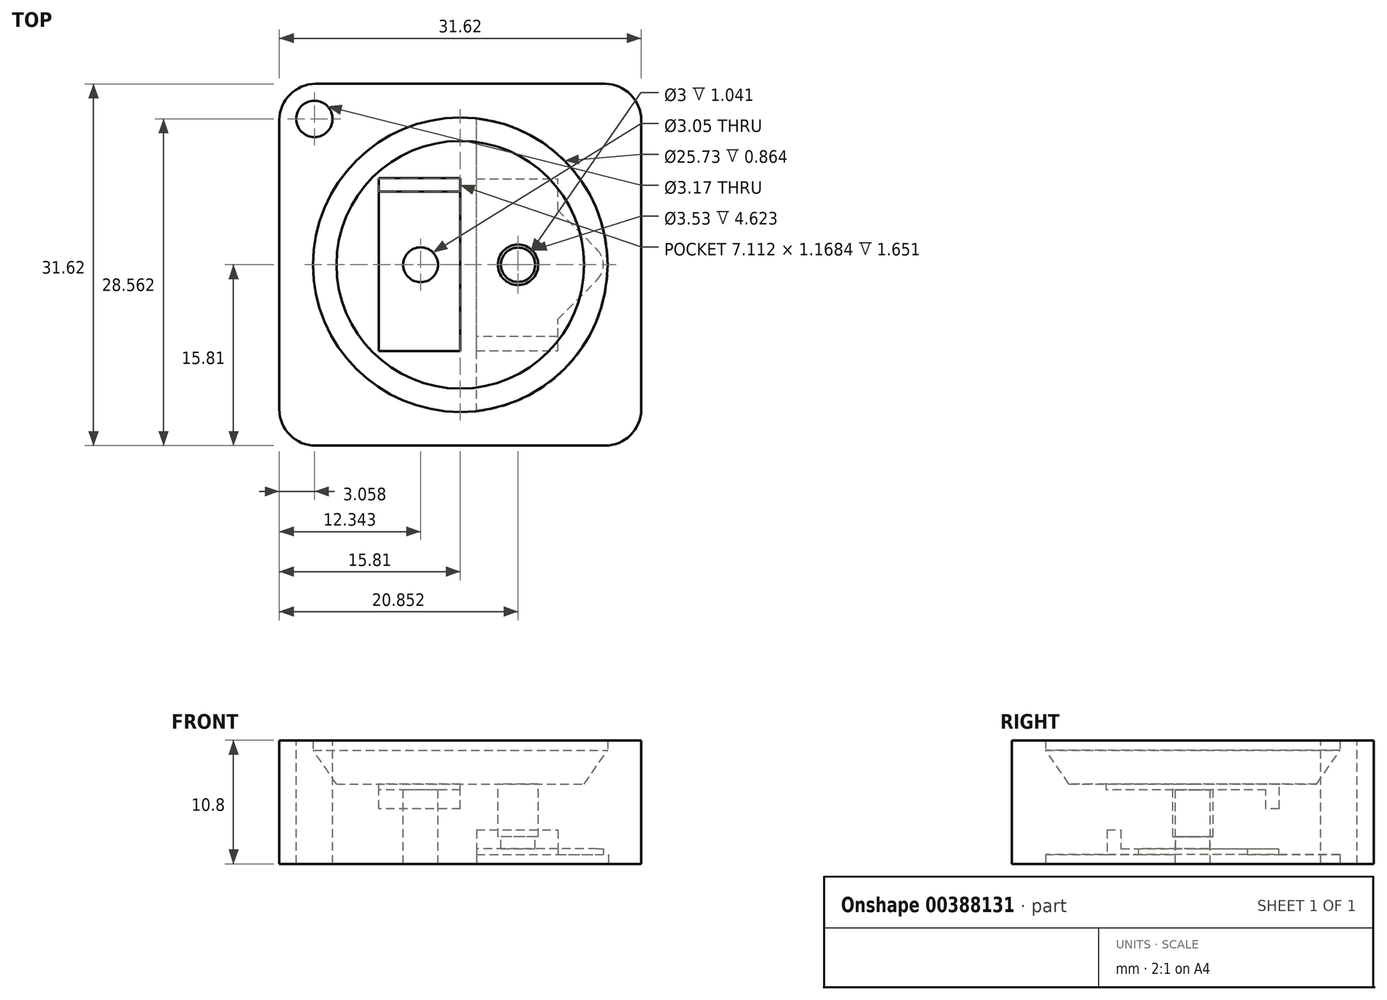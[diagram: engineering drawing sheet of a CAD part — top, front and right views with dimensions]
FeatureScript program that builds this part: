
annotation { "Feature Type Name" : "Feature", "Feature Type Description" : "" }
export const myFeature = defineFeature(function(context is Context, id is Id, definition is map)
    precondition{}
    {
        {
            var Q0;
            Q0=qCreatedBy(makeId("Top.planeOp"),FACE);
            var sketch = newSketch(context, id + "F0", { "sketchPlane" : qUnion([Q0])});
            skLineSegment(sketch, "E0.bottom", {"start": v(-12.64, 15.81) * mm, "end": v(12.64, 15.81) * mm});
            skLineSegment(sketch, "E0.top", {"start": v(-12.64, -15.81) * mm, "end": v(12.64, -15.81) * mm});
            skLineSegment(sketch, "E0.left", {"start": v(-15.81, 12.64) * mm, "end": v(-15.81, -12.64) * mm});
            skLineSegment(sketch, "E0.right", {"start": v(15.81, 12.64) * mm, "end": v(15.81, -12.64) * mm});
            skArc(sketch, "E1.filletArc", {"start": v(15.81, 12.64) * mm, "mid": v(14.88, 14.88) * mm, "end": v(12.64, 15.81) * mm});
            skArc(sketch, "E2.filletArc", {"start": v(12.64, -15.81) * mm, "mid": v(14.88, -14.88) * mm, "end": v(15.81, -12.64) * mm});
            skArc(sketch, "E3.filletArc", {"start": v(-15.81, -12.64) * mm, "mid": v(-14.88, -14.88) * mm, "end": v(-12.64, -15.81) * mm});
            skPoint(sketch, "E4.visualSharp", {"position": v(0, 15.81) * mm});
            skArc(sketch, "E4.filletArc", {"start": v(-12.64, 15.81) * mm, "mid": v(-14.88, 14.88) * mm, "end": v(-15.81, 12.64) * mm});
            skLineSegment(sketch, "E5", {"start": v(-15.81, 15.81) * mm, "end": v(15.81, -15.81) * mm, "construction": true});
            skSolve(sketch);
        }
        {
            var Q0;
            Q0 = qSketchRegion(id + "F0", true);
            extrude(context, id + "F1", {"entities" : qUnion([Q0]), "depth" : 10.8 * mm});
        }
        {
            var Q0;
            Q0=qCreatedBy(makeId("Front.planeOp"),FACE);
            var sketch = newSketch(context, id + "F2", { "sketchPlane" : qUnion([Q0])});
            skLineSegment(sketch, "E6", {"start": v(0, 19.76) * mm, "end": v(0, -16.76) * mm, "construction": true});
            skLineSegment(sketch, "E7", {"start": v(0, 6.99) * mm, "end": v(10.82, 6.99) * mm});
            skLineSegment(sketch, "E8", {"start": v(10.82, 6.98) * mm, "end": v(12.87, 9.93) * mm});
            skLineSegment(sketch, "E9", {"start": v(12.87, 9.93) * mm, "end": v(12.87, 10.8) * mm});
            skLineSegment(sketch, "E10", {"start": v(12.87, 10.8) * mm, "end": v(0, 10.8) * mm});
            skLineSegment(sketch, "E11", {"start": v(0, 10.8) * mm, "end": v(0, 6.98) * mm});
            skSolve(sketch);
        }
        {
            var Q0;
            Q0 = qSketchRegion(id + "F2", true);
            var Q1;
            Q1=sQuery(id+"F2.wireOp",EDGE,"E6");
            revolve(context, id + "F3", {"operationType" : NewBodyOperationType.REMOVE, "entities" : qUnion([Q0]), "axis" : qUnion([Q1]), "revolveType" : RevolveType.FULL, "oppositeDirection" : true});
        }
        {
            var Q0;
            Q0=makeQuery(id+"F1.opExtrude","CAP_FACE",FACE,{"disambiguationData":[OSD([sQuery(id+"F0.wireOp",EDGE,"E0.bottom"),sQuery(id+"F0.wireOp",EDGE,"E0.top"),sQuery(id+"F0.wireOp",EDGE,"E0.left"),sQuery(id+"F0.wireOp",EDGE,"E0.right"),sQuery(id+"F0.wireOp",EDGE,"E1.filletArc"),sQuery(id+"F0.wireOp",EDGE,"E2.filletArc"),sQuery(id+"F0.wireOp",EDGE,"E3.filletArc"),sQuery(id+"F0.wireOp",EDGE,"E4.filletArc")])],"isStart":false});
            var sketch = newSketch(context, id + "F4", { "sketchPlane" : qUnion([Q0])});
            skPoint(sketch, "E12", {"position": v(-12.75, 12.75) * mm});
            skLineSegment(sketch, "E13", {"start": v(0, 15.81) * mm, "end": v(0, -15.81) * mm, "construction": true});
            skPoint(sketch, "E14", {"position": v(0, 0) * mm});
            skLineSegment(sketch, "E15", {"start": v(-15.81, 15.81) * mm, "end": v(15.81, -15.81) * mm, "construction": true});
            skSolve(sketch);
        }
        {
            var Q0;
            Q0=sQuery(id+"F4.wireOp",VERTEX,"E12");
            var Q1;
            Q1=makeQuery(id+"F1.opExtrude","SWEPT_BODY",BODY,{"disambiguationData":[OSD([sQuery(id+"F0.wireOp",EDGE,"E0.bottom"),sQuery(id+"F0.wireOp",EDGE,"E0.top"),sQuery(id+"F0.wireOp",EDGE,"E0.left"),sQuery(id+"F0.wireOp",EDGE,"E0.right"),sQuery(id+"F0.wireOp",EDGE,"E1.filletArc"),sQuery(id+"F0.wireOp",EDGE,"E2.filletArc"),sQuery(id+"F0.wireOp",EDGE,"E3.filletArc"),sQuery(id+"F0.wireOp",EDGE,"E4.filletArc")])]});
            hole(context, id + "F5", {"style" : HoleStyle.SIMPLE, "endStyle" : HoleEndStyle.THROUGH, "holeDiameter" : 3.17 * mm, "isTappedThrough" : true, "tappedDepth" : 12.7 * mm, "tapClearance" : 3, "locations" : qUnion([Q0]), "scope" : qUnion([Q1])});
        }
        {
            var Q0;
            Q0=makeQuery(id+"F3.boolean.opBoolean","COPY",FACE,{"derivedFrom":makeQuery(id+"F3.opRevolve","SWEPT_FACE",FACE,{"disambiguationData":[OSD([sQuery(id+"F2.wireOp",EDGE,"E7")])]})});
            var sketch = newSketch(context, id + "F6", { "sketchPlane" : qUnion([Q0])});
            skPoint(sketch, "E16", {"position": v(5.04, 0) * mm});
            skSolve(sketch);
        }
        {
            var Q0;
            Q0=sQuery(id+"F6.wireOp",VERTEX,"E16");
            var Q1;
            Q1=makeQuery(id+"F1.opExtrude","SWEPT_BODY",BODY,{"disambiguationData":[OSD([sQuery(id+"F0.wireOp",EDGE,"E0.bottom"),sQuery(id+"F0.wireOp",EDGE,"E0.top"),sQuery(id+"F0.wireOp",EDGE,"E0.left"),sQuery(id+"F0.wireOp",EDGE,"E0.right"),sQuery(id+"F0.wireOp",EDGE,"E1.filletArc"),sQuery(id+"F0.wireOp",EDGE,"E2.filletArc"),sQuery(id+"F0.wireOp",EDGE,"E3.filletArc"),sQuery(id+"F0.wireOp",EDGE,"E4.filletArc")])]});
            hole(context, id + "F7", {"style" : HoleStyle.C_BORE, "endStyle" : HoleEndStyle.THROUGH, "holeDiameter" : 3 * mm, "cBoreDiameter" : 3.53 * mm, "cBoreDepth" : 4.62 * mm, "isTappedThrough" : true, "tappedDepth" : 12.7 * mm, "tapClearance" : 3, "locations" : qUnion([Q0]), "scope" : qUnion([Q1])});
        }
        {
            var Q0;
            Q0=makeQuery(id+"F3.boolean.opBoolean","COPY",FACE,{"derivedFrom":makeQuery(id+"F3.opRevolve","SWEPT_FACE",FACE,{"disambiguationData":[OSD([sQuery(id+"F2.wireOp",EDGE,"E7")])]})});
            var sketch = newSketch(context, id + "F8", { "sketchPlane" : qUnion([Q0])});
            skPoint(sketch, "E17", {"position": v(-3.47, 0) * mm});
            skSolve(sketch);
        }
        {
            var Q0;
            Q0=sQuery(id+"F8.wireOp",VERTEX,"E17");
            var Q1;
            Q1=makeQuery(id+"F1.opExtrude","SWEPT_BODY",BODY,{"disambiguationData":[OSD([sQuery(id+"F0.wireOp",EDGE,"E0.bottom"),sQuery(id+"F0.wireOp",EDGE,"E0.top"),sQuery(id+"F0.wireOp",EDGE,"E0.left"),sQuery(id+"F0.wireOp",EDGE,"E0.right"),sQuery(id+"F0.wireOp",EDGE,"E1.filletArc"),sQuery(id+"F0.wireOp",EDGE,"E2.filletArc"),sQuery(id+"F0.wireOp",EDGE,"E3.filletArc"),sQuery(id+"F0.wireOp",EDGE,"E4.filletArc")])]});
            hole(context, id + "F9", {"style" : HoleStyle.SIMPLE, "endStyle" : HoleEndStyle.THROUGH, "holeDiameter" : 3.05 * mm, "isTappedThrough" : true, "tappedDepth" : 12.7 * mm, "tapClearance" : 3, "locations" : qUnion([Q0]), "scope" : qUnion([Q1])});
        }
        {
            var Q0;
            Q0=makeQuery(id+"F3.boolean.opBoolean","COPY",FACE,{"derivedFrom":makeQuery(id+"F3.opRevolve","SWEPT_FACE",FACE,{"disambiguationData":[OSD([sQuery(id+"F2.wireOp",EDGE,"E7")])]})});
            var sketch = newSketch(context, id + "F10", { "sketchPlane" : qUnion([Q0])});
            skLineSegment(sketch, "E18.bottom", {"start": v(0, 7.56) * mm, "end": v(-7.11, 7.56) * mm});
            skLineSegment(sketch, "E18.top", {"start": v(0, -7.56) * mm, "end": v(-7.11, -7.56) * mm});
            skLineSegment(sketch, "E18.left", {"start": v(0, 7.56) * mm, "end": v(0, -7.56) * mm});
            skLineSegment(sketch, "E18.right", {"start": v(-7.11, 7.56) * mm, "end": v(-7.11, -7.56) * mm});
            skSolve(sketch);
        }
        {
            var Q0;
            Q0 = qSketchRegion(id + "F10", true);
            extrude(context, id + "F11", {"entities" : qUnion([Q0]), "operationType" : NewBodyOperationType.REMOVE, "oppositeDirection" : true, "depth" : 0.5 * mm});
        }
        {
            var Q0;
            Q0=makeQuery(id+"F3.boolean.opBoolean","COPY",FACE,{"derivedFrom":makeQuery(id+"F3.opRevolve","SWEPT_FACE",FACE,{"disambiguationData":[OSD([sQuery(id+"F2.wireOp",EDGE,"E7")])]})});
            var sketch = newSketch(context, id + "F12", { "sketchPlane" : qUnion([Q0])});
            skLineSegment(sketch, "E19.bottom", {"start": v(0, 7.56) * mm, "end": v(-7.11, 7.56) * mm});
            skLineSegment(sketch, "E19.top", {"start": v(0, 6.39) * mm, "end": v(-7.11, 6.39) * mm});
            skLineSegment(sketch, "E19.left", {"start": v(0, 7.56) * mm, "end": v(0, 6.39) * mm});
            skLineSegment(sketch, "E19.right", {"start": v(-7.11, 7.56) * mm, "end": v(-7.11, 6.39) * mm});
            skSolve(sketch);
        }
        {
            var Q0;
            Q0 = qSketchRegion(id + "F12", true);
            extrude(context, id + "F13", {"entities" : qUnion([Q0]), "operationType" : NewBodyOperationType.REMOVE, "oppositeDirection" : true, "depth" : 2.16 * mm});
        }
        {
            var Q0;
            Q0=makeQuery(id+"F1.opExtrude","CAP_FACE",FACE,{"disambiguationData":[OSD([sQuery(id+"F0.wireOp",EDGE,"E0.bottom"),sQuery(id+"F0.wireOp",EDGE,"E0.top"),sQuery(id+"F0.wireOp",EDGE,"E0.left"),sQuery(id+"F0.wireOp",EDGE,"E0.right"),sQuery(id+"F0.wireOp",EDGE,"E1.filletArc"),sQuery(id+"F0.wireOp",EDGE,"E2.filletArc"),sQuery(id+"F0.wireOp",EDGE,"E3.filletArc"),sQuery(id+"F0.wireOp",EDGE,"E4.filletArc")])],"isStart":true});
            var sketch = newSketch(context, id + "F14", { "sketchPlane" : qUnion([Q0])});
            skLineSegment(sketch, "E20", {"start": v(1.4, 12.85) * mm, "end": v(1.4, -12.85) * mm});
            skArc(sketch, "E21", {"start": v(1.4, -12.85) * mm, "mid": v(12.94, 0) * mm, "end": v(1.4, 12.85) * mm});
            skSolve(sketch);
        }
        {
            var Q0;
            Q0 = qSketchRegion(id + "F14", true);
            extrude(context, id + "F15", {"entities" : qUnion([Q0]), "operationType" : NewBodyOperationType.REMOVE, "oppositeDirection" : true, "depth" : 0.81 * mm});
        }
        {
            var Q0;
            Q0=makeQuery(id+"F15.boolean.opBoolean","COPY",FACE,{"derivedFrom":makeQuery(id+"F15.opExtrude","CAP_FACE",FACE,{"disambiguationData":[OSD([sQuery(id+"F14.wireOp",EDGE,"E20"),sQuery(id+"F14.wireOp",EDGE,"E21")])],"isStart":false})});
            var sketch = newSketch(context, id + "F16", { "sketchPlane" : qUnion([Q0])});
            skLineSegment(sketch, "E22.bottom", {"start": v(1.4, 7.5) * mm, "end": v(8.52, 7.5) * mm});
            skLineSegment(sketch, "E22.top", {"start": v(1.4, -7.5) * mm, "end": v(8.52, -7.5) * mm});
            skLineSegment(sketch, "E22.left", {"start": v(1.4, 7.5) * mm, "end": v(1.4, -7.5) * mm});
            skLineSegment(sketch, "E22.right", {"start": v(8.52, 7.5) * mm, "end": v(8.52, -7.5) * mm});
            skPoint(sketch, "E23", {"position": v(8.52, 0) * mm});
            skSolve(sketch);
        }
        {
            var Q0;
            Q0 = qSketchRegion(id + "F16", true);
            extrude(context, id + "F17", {"entities" : qUnion([Q0]), "operationType" : NewBodyOperationType.REMOVE, "oppositeDirection" : true, "depth" : 0.5 * mm});
        }
        {
            var Q0;
            Q0=makeQuery(id+"F15.boolean.opBoolean","COPY",FACE,{"derivedFrom":makeQuery(id+"F15.opExtrude","CAP_FACE",FACE,{"disambiguationData":[OSD([sQuery(id+"F14.wireOp",EDGE,"E20"),sQuery(id+"F14.wireOp",EDGE,"E21")])],"isStart":false})});
            var sketch = newSketch(context, id + "F18", { "sketchPlane" : qUnion([Q0])});
            skLineSegment(sketch, "E24.bottom", {"start": v(8.52, 7.5) * mm, "end": v(1.4, 7.5) * mm});
            skLineSegment(sketch, "E24.top", {"start": v(8.52, 6.29) * mm, "end": v(1.4, 6.29) * mm});
            skLineSegment(sketch, "E24.left", {"start": v(8.52, 7.5) * mm, "end": v(8.52, 6.29) * mm});
            skLineSegment(sketch, "E24.right", {"start": v(1.4, 7.5) * mm, "end": v(1.4, 6.29) * mm});
            skSolve(sketch);
        }
        {
            var Q0;
            Q0 = qSketchRegion(id + "F18", true);
            extrude(context, id + "F19", {"entities" : qUnion([Q0]), "operationType" : NewBodyOperationType.REMOVE, "oppositeDirection" : true, "depth" : 2.16 * mm});
        }
        {
            var Q0;
            Q0=makeQuery(id+"F15.boolean.opBoolean","COPY",FACE,{"derivedFrom":makeQuery(id+"F15.opExtrude","CAP_FACE",FACE,{"disambiguationData":[OSD([sQuery(id+"F14.wireOp",EDGE,"E20"),sQuery(id+"F14.wireOp",EDGE,"E21")])],"isStart":false})});
            var sketch = newSketch(context, id + "F20", { "sketchPlane" : qUnion([Q0])});
            skLineSegment(sketch, "E25", {"start": v(8.52, 4.76) * mm, "end": v(8.52, -4.76) * mm});
            skPoint(sketch, "E26", {"position": v(8.52, 0) * mm});
            skLineSegment(sketch, "E27", {"start": v(8.52, 4.76) * mm, "end": v(11.94, 1.35) * mm});
            skLineSegment(sketch, "E28", {"start": v(8.52, -4.76) * mm, "end": v(11.94, -1.35) * mm});
            skArc(sketch, "E29.0", {"start": v(11.94, -1.35) * mm, "mid": v(12.5, 0) * mm, "end": v(11.94, 1.35) * mm});
            skLineSegment(sketch, "E30", {"start": v(-7.7, 0) * mm, "end": v(21.37, 0) * mm, "construction": true});
            skSolve(sketch);
        }
        {
            var Q0;
            Q0 = qSketchRegion(id + "F20", true);
            var Q1;
            Q1 = qConstructionFilter(qBodyType(qCreatedBy(id + "F20" ,EDGE), BodyType.WIRE), ConstructionObject.NO);
            var Q2;
            Q2=makeQuery(id+"F17.boolean.opBoolean","COPY",FACE,{"derivedFrom":makeQuery(id+"F17.opExtrude","CAP_FACE",FACE,{"disambiguationData":[OSD([sQuery(id+"F16.wireOp",EDGE,"E22.bottom"),sQuery(id+"F16.wireOp",EDGE,"E22.top"),sQuery(id+"F16.wireOp",EDGE,"E22.left"),sQuery(id+"F16.wireOp",EDGE,"E22.right")])],"isStart":false})});
            extrude(context, id + "F21", {"entities" : qUnion([Q0]), "operationType" : NewBodyOperationType.REMOVE, "surfaceEntities" : qUnion([Q1]), "endBound" : BoundingType.UP_TO_SURFACE, "oppositeDirection" : true, "endBoundEntityFace" : qUnion([Q2]), "depth" : 0.5 * mm});
        }
    });
